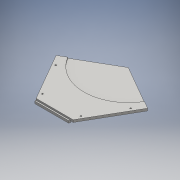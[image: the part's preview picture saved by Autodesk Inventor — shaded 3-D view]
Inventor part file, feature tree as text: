
AUTODESK INVENTOR PART (.ipt)
format: ipt  version: 2016 SP1 (Build 200210100, 210)  size: 253,440 bytes
history: native  units: mm
features: extrude x3, sketch x3, reference x3
ambient origin geometry x8: Origin, YZ Plane, XZ Plane, XY Plane, X Axis, Y Axis, Z Axis, Center Point
bodies: Solid1 (feature_tree)
feature tree (9):
  extrude  "Extrusion1"  Depth=5.0mm
  extrude  "Extrusion2"  Depth=5.0mm
  extrude  "Extrusion3"  Depth=10.0mm
  sketch  "Sketch1"  dims[d0=5.0mm d1=5.0mm]
  reference  "Reference2"
  reference  "Reference3"
  sketch  "Sketch2"  dims[d2=5.0mm d3=5.0mm]
  reference  "Reference4"
  sketch  "Sketch3"  dims[d4=10.0mm d5=10.0mm d6=10.0mm d7=10.0mm d8=40.0mm d9=40.0mm d10=125.0mm d11=125.0mm d12=8.0mm d13=0.0mm d14=3.0mm d15=0.0mm d16=10.0mm d18=3.0mm d19=0.0mm]
